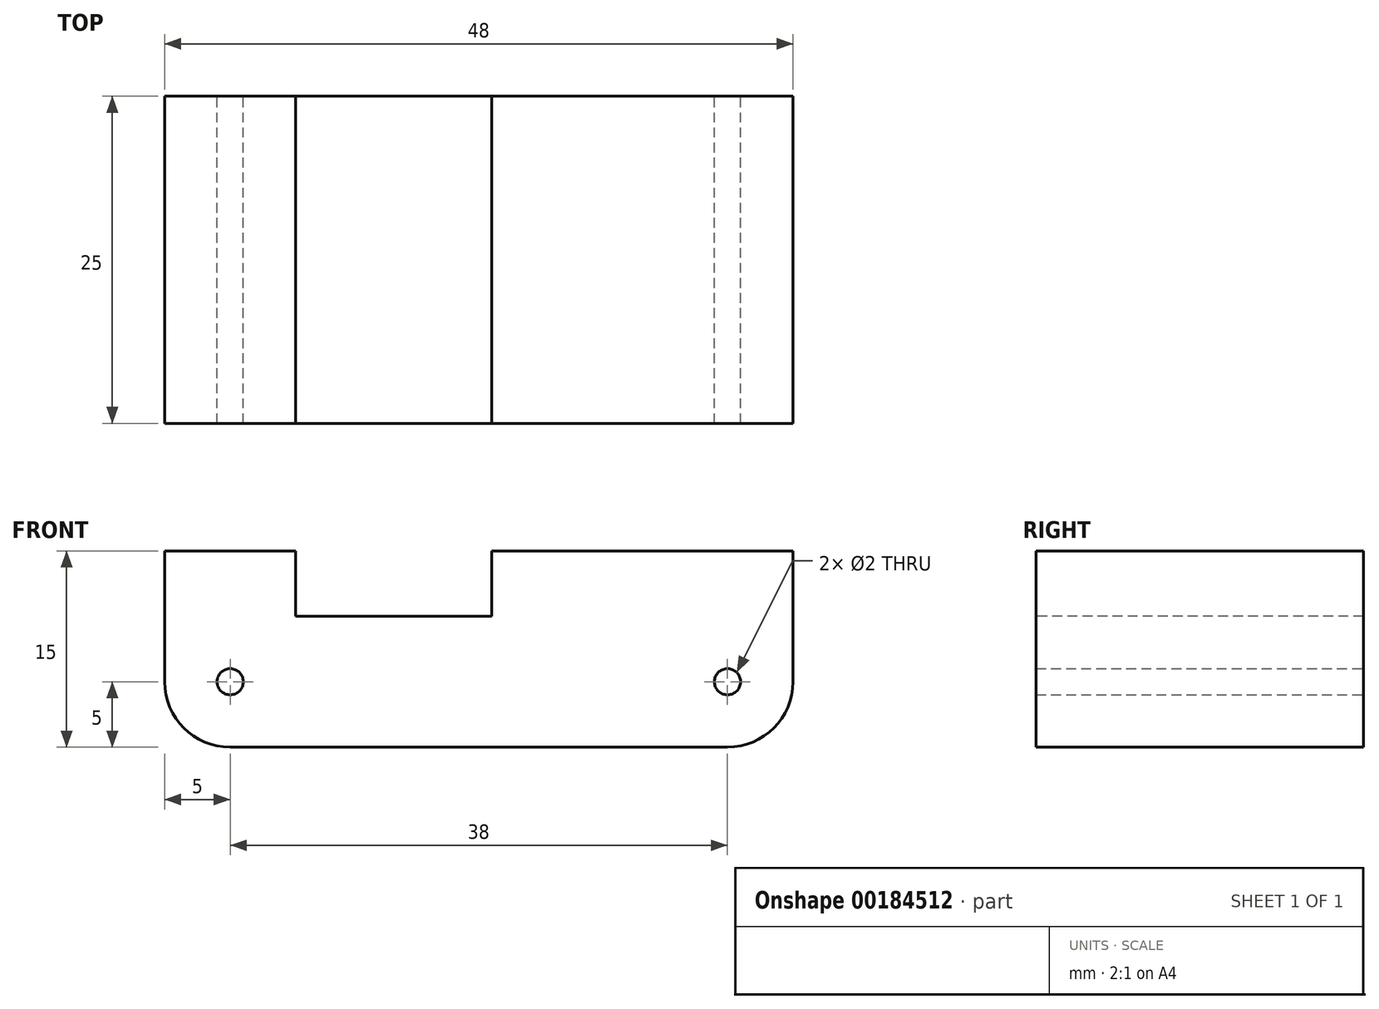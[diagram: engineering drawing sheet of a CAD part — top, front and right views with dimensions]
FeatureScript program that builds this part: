
annotation { "Feature Type Name" : "Feature", "Feature Type Description" : "" }
export const myFeature = defineFeature(function(context is Context, id is Id, definition is map)
    precondition{}
    {
        {
            var Q0;
            Q0=qCreatedBy(makeId("Front.planeOp"),FACE);
            var sketch = newSketch(context, id + "F0", { "sketchPlane" : qUnion([Q0])});
            skLineSegment(sketch, "E0.bottom", {"start": v(0, 0) * mm, "end": v(48, 0) * mm});
            skLineSegment(sketch, "E0.top", {"start": v(0, -15) * mm, "end": v(48, -15) * mm});
            skLineSegment(sketch, "E0.left", {"start": v(0, 0) * mm, "end": v(0, -15) * mm});
            skLineSegment(sketch, "E0.right", {"start": v(48, 0) * mm, "end": v(48, -15) * mm});
            skCircle(sketch, "E1", {"center": v(5, -10) * mm, "radius": 1 * mm});
            skCircle(sketch, "E2", {"center": v(43, -10) * mm, "radius": 1 * mm});
            skSolve(sketch);
        }
        {
            var Q0;
            Q0 = qSketchRegion(id + "F0", true);
            extrude(context, id + "F1", {"entities" : qUnion([Q0]), "depth" : 25 * mm});
        }
        {
            var Q0;
            Q0=makeQuery(id+"F1.opExtrude","SWEPT_EDGE",EDGE,{"disambiguationData":[OSD([sQuery(id+"F0.wireOp",EDGE,"E0.top"),sQuery(id+"F0.wireOp",EDGE,"E0.left")])]});
            var Q1;
            Q1=makeQuery(id+"F1.opExtrude","SWEPT_EDGE",EDGE,{"disambiguationData":[OSD([sQuery(id+"F0.wireOp",EDGE,"E0.top"),sQuery(id+"F0.wireOp",EDGE,"E0.right")])]});
            fillet(context, id + "F2", {"entities" : qUnion([Q0, Q1]), "radius" : 5 * mm, "tangentPropagation" : true, "allowEdgeOverflow" : false});
        }
        {
            var Q0;
            Q0=makeQuery(id+"F1.opExtrude","SWEPT_FACE",FACE,{"disambiguationData":[OSD([sQuery(id+"F0.wireOp",EDGE,"E0.bottom")])]});
            var sketch = newSketch(context, id + "F3", { "sketchPlane" : qUnion([Q0])});
            skLineSegment(sketch, "E3.bottom", {"start": v(10, 0) * mm, "end": v(25, 0) * mm});
            skLineSegment(sketch, "E3.top", {"start": v(10, -25) * mm, "end": v(25, -25) * mm});
            skLineSegment(sketch, "E3.left", {"start": v(10, 0) * mm, "end": v(10, -25) * mm});
            skLineSegment(sketch, "E3.right", {"start": v(25, 0) * mm, "end": v(25, -25) * mm});
            skSolve(sketch);
        }
        {
            var Q0;
            Q0=makeQuery(id+"F3.imprint","IMPRINT",FACE,{"disambiguationData":[TD([[makeQuery(id+"F3.imprint","IMPRINT",EDGE,{"derivedFrom":sQuery(id+"F3.wireOp",EDGE,"E3.bottom")}),-1.0]])]});
            extrude(context, id + "F4", {"entities" : qUnion([Q0]), "operationType" : NewBodyOperationType.REMOVE, "oppositeDirection" : true, "depth" : 5 * mm});
        }
    });
